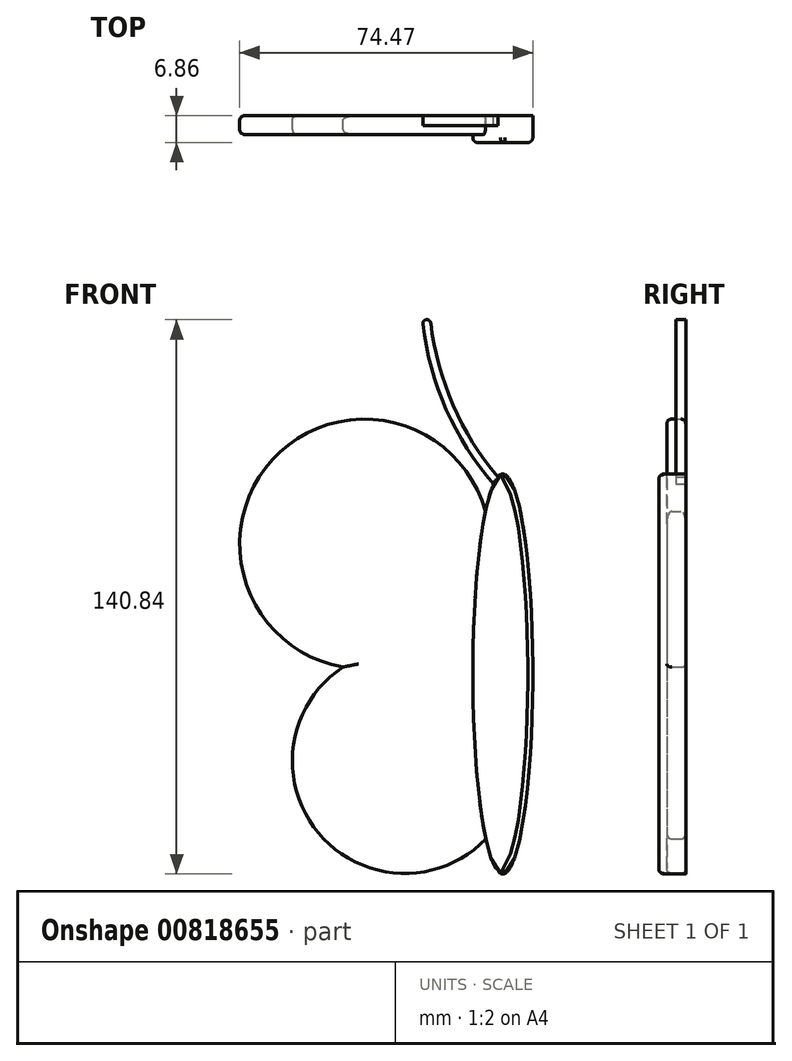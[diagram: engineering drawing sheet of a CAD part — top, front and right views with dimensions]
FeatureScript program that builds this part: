
annotation { "Feature Type Name" : "Feature", "Feature Type Description" : "" }
export const myFeature = defineFeature(function(context is Context, id is Id, definition is map)
    precondition{}
    {
        {
            var Q0;
            Q0=qCreatedBy(makeId("Front.planeOp"),FACE);
            var sketch = newSketch(context, id + "F0", { "sketchPlane" : qUnion([Q0])});
            skEllipse(sketch, "E0", {"center": v(0, 0) * mm, "majorRadius": 50.8 * mm, "minorRadius": 7.62 * mm, "majorAxis": v(0, -1)});
            skArc(sketch, "E1", {"start": v(-4.44, 41.27) * mm, "mid": v(-58.51, 54.47) * mm, "end": v(-40.64, 1.76) * mm});
            skArc(sketch, "E2", {"start": v(-40.64, 1.76) * mm, "mid": v(-46.84, -40.35) * mm, "end": v(-4.3, -41.91) * mm});
            skArc(sketch, "E3.MirrorCS", {"start": v(4.44, 41.27) * mm, "mid": v(58.51, 54.47) * mm, "end": v(40.64, 1.76) * mm});
            skArc(sketch, "E4.MirrorCS", {"start": v(40.64, 1.76) * mm, "mid": v(46.84, -40.35) * mm, "end": v(4.3, -41.91) * mm});
            skArc(sketch, "E5", {"start": v(-20.32, 88.9) * mm, "mid": v(-14.38, 67.24) * mm, "end": v(-2.38, 48.26) * mm});
            skArc(sketch, "E6.0", {"start": v(-18.3, 89.14) * mm, "mid": v(-12.65, 68.37) * mm, "end": v(-1.27, 50.09) * mm});
            skArc(sketch, "E7", {"start": v(-18.3, 89.14) * mm, "mid": v(-19.43, 90.03) * mm, "end": v(-20.32, 88.9) * mm});
            skArc(sketch, "E8.MirrorCS", {"start": v(18.3, 89.14) * mm, "mid": v(12.65, 68.37) * mm, "end": v(1.27, 50.09) * mm});
            skArc(sketch, "E9.MirrorCS", {"start": v(20.32, 88.9) * mm, "mid": v(14.38, 67.24) * mm, "end": v(2.38, 48.26) * mm});
            skArc(sketch, "E10.MirrorCS", {"start": v(18.3, 89.14) * mm, "mid": v(19.43, 90.03) * mm, "end": v(20.32, 88.9) * mm});
            skSolve(sketch);
        }
        {
            var Q0;
            {var subQ0=sQuery(id+"F0.wireOp",EDGE,"E0");var subQ4=makeQuery(id+"F0.imprint","INTERSECT",VERTEX,{"derivedFrom":[subQ0,sQuery(id+"F0.wireOp",EDGE,"E3.MirrorCS")]});Q0=makeQuery(id+"F0.imprint","IMPRINT",FACE,{"disambiguationData":[TD([[makeQuery(id+"F0.imprint","IMPRINT",EDGE,{"disambiguationData":[TD([[subQ4,1.0]])],"derivedFrom":subQ0}),1.0]])]});}
            extrude(context, id + "F1", {"entities" : qUnion([Q0]), "depth" : 6.86 * mm, "offsetDistance" : 25.4 * mm});
        }
        {
            var Q0;
            {var subQ0=sQuery(id+"F0.wireOp",EDGE,"E3.MirrorCS");Q0=makeQuery(id+"F0.imprint","IMPRINT",FACE,{"disambiguationData":[TD([[makeQuery(id+"F0.imprint","IMPRINT",EDGE,{"derivedFrom":subQ0}),-1.0]])]});}
            var Q1;
            {var subQ0=sQuery(id+"F0.wireOp",EDGE,"E1");Q1=makeQuery(id+"F0.imprint","IMPRINT",FACE,{"disambiguationData":[TD([[makeQuery(id+"F0.imprint","IMPRINT",EDGE,{"derivedFrom":subQ0}),1.0]])]});}
            extrude(context, id + "F2", {"entities" : qUnion([Q0, Q1]), "operationType" : NewBodyOperationType.ADD, "depth" : 4.83 * mm, "offsetDistance" : 25.4 * mm});
        }
        {
            var Q0;
            {var subQ0=sQuery(id+"F0.wireOp",EDGE,"E5");Q0=makeQuery(id+"F0.imprint","IMPRINT",FACE,{"disambiguationData":[TD([[makeQuery(id+"F0.imprint","IMPRINT",EDGE,{"derivedFrom":subQ0}),1.0]])]});}
            var Q1;
            {var subQ0=sQuery(id+"F0.wireOp",EDGE,"E8.MirrorCS");Q1=makeQuery(id+"F0.imprint","IMPRINT",FACE,{"disambiguationData":[TD([[makeQuery(id+"F0.imprint","IMPRINT",EDGE,{"derivedFrom":subQ0}),1.0]])]});}
            extrude(context, id + "F3", {"entities" : qUnion([Q0, Q1]), "operationType" : NewBodyOperationType.ADD, "depth" : 2.54 * mm, "offsetDistance" : 25.4 * mm});
        }
        {
            var Q0;
            Q0=makeQuery(id+"F2.opExtrude","CAP_EDGE",EDGE,{"disambiguationData":[OSD([sQuery(id+"F0.wireOp",EDGE,"E1")])],"isStart":false});
            var Q1;
            Q1=makeQuery(id+"F2.opExtrude","CAP_EDGE",EDGE,{"disambiguationData":[OSD([sQuery(id+"F0.wireOp",EDGE,"E2")])],"isStart":false});
            var Q2;
            Q2=makeQuery(id+"F2.opExtrude","CAP_EDGE",EDGE,{"disambiguationData":[OSD([sQuery(id+"F0.wireOp",EDGE,"E4.MirrorCS")])],"isStart":false});
            var Q3;
            Q3=makeQuery(id+"F2.opExtrude","CAP_EDGE",EDGE,{"disambiguationData":[OSD([sQuery(id+"F0.wireOp",EDGE,"E3.MirrorCS")])],"isStart":false});
            var Q4;
            Q4=makeQuery(id+"F2.opExtrude","CAP_EDGE",EDGE,{"disambiguationData":[OSD([sQuery(id+"F0.wireOp",EDGE,"E3.MirrorCS")])],"isStart":true});
            var Q5;
            Q5=makeQuery(id+"F2.opExtrude","CAP_EDGE",EDGE,{"disambiguationData":[OSD([sQuery(id+"F0.wireOp",EDGE,"E4.MirrorCS")])],"isStart":true});
            var Q6;
            Q6=makeQuery(id+"F2.opExtrude","CAP_EDGE",EDGE,{"disambiguationData":[OSD([sQuery(id+"F0.wireOp",EDGE,"E2")])],"isStart":true});
            var Q7;
            Q7=makeQuery(id+"F2.opExtrude","CAP_EDGE",EDGE,{"disambiguationData":[OSD([sQuery(id+"F0.wireOp",EDGE,"E1")])],"isStart":true});
            fillet(context, id + "F4", {"entities" : qUnion([Q0, Q1, Q2, Q3, Q4, Q5, Q6, Q7]), "radius" : 1.27 * mm, "tangentPropagation" : true, "allowEdgeOverflow" : false});
        }
        {
            var Q0;
            Q0=makeQuery(id+"F1.opExtrude","CAP_EDGE",EDGE,{"disambiguationData":[OSD([sQuery(id+"F0.wireOp",EDGE,"E0")])],"isStart":false});
            fillet(context, id + "F5", {"entities" : qUnion([Q0]), "radius" : 1.27 * mm, "tangentPropagation" : true, "allowEdgeOverflow" : false});
        }
    });
